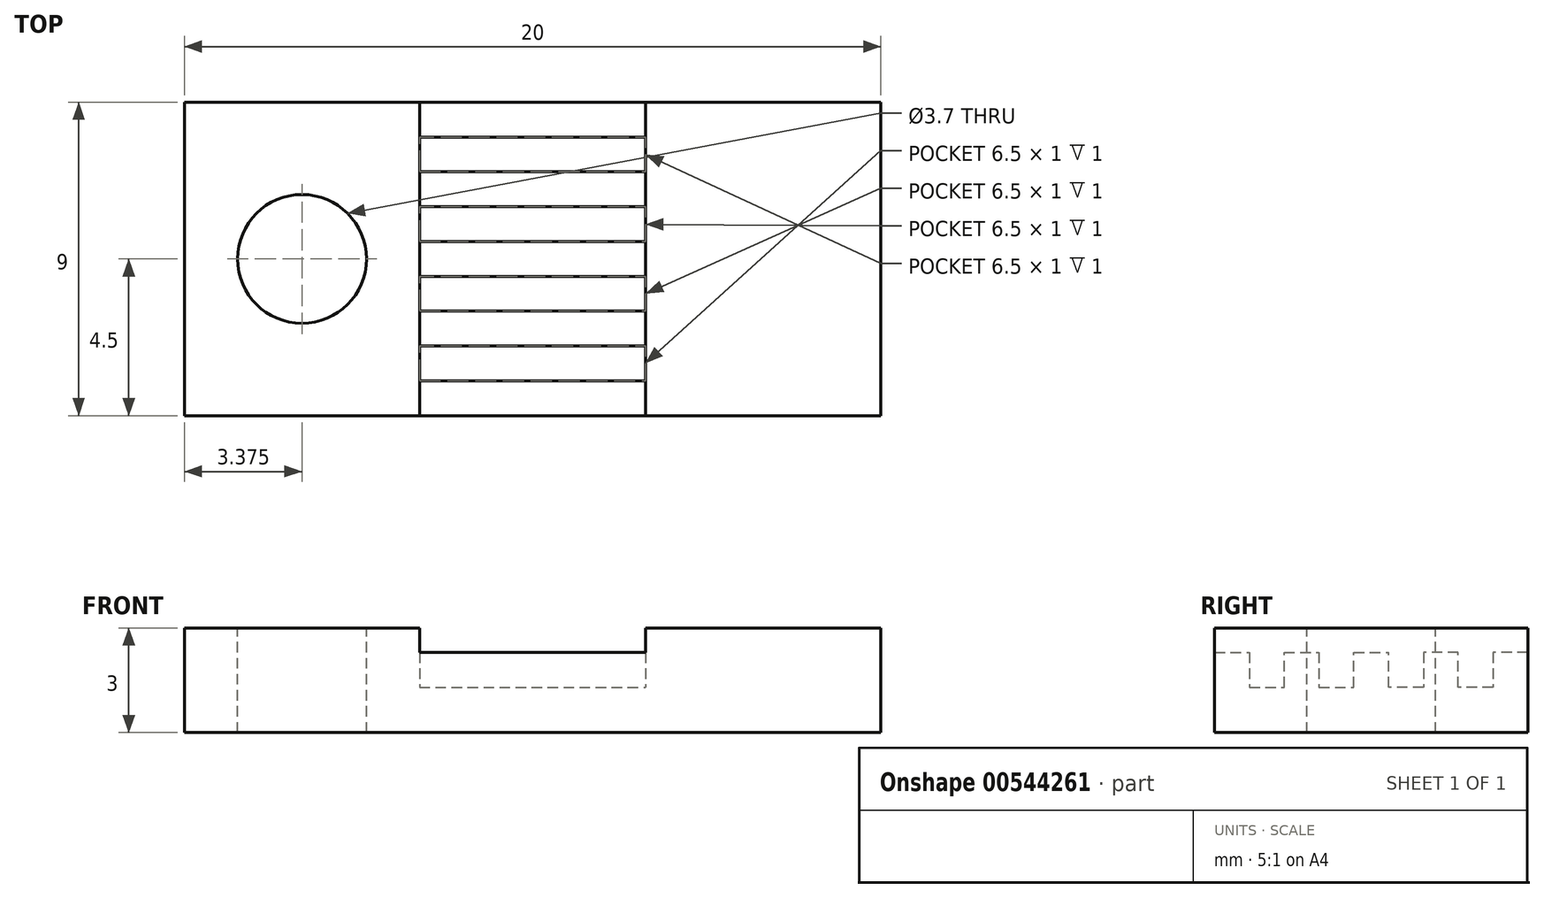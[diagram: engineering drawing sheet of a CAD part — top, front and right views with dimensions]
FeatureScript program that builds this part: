
annotation { "Feature Type Name" : "Feature", "Feature Type Description" : "" }
export const myFeature = defineFeature(function(context is Context, id is Id, definition is map)
    precondition{}
    {
        {
            var Q0;
            Q0=qCreatedBy(makeId("Top.planeOp"),FACE);
            var sketch = newSketch(context, id + "F0", { "sketchPlane" : qUnion([Q0])});
            skLineSegment(sketch, "E0.bottom", {"start": v(10, 4.5) * mm, "end": v(-10, 4.5) * mm});
            skLineSegment(sketch, "E0.top", {"start": v(10, -4.5) * mm, "end": v(-10, -4.5) * mm});
            skLineSegment(sketch, "E0.left", {"start": v(10, 4.5) * mm, "end": v(10, -4.5) * mm});
            skLineSegment(sketch, "E0.right", {"start": v(-10, 4.5) * mm, "end": v(-10, -4.5) * mm});
            skPoint(sketch, "E0.middle", {"position": v(0, 0) * mm});
            skSolve(sketch);
        }
        {
            var Q0;
            Q0=makeQuery(id+"F0.imprint","IMPRINT",FACE,{"disambiguationData":[TD([[makeQuery(id+"F0.imprint","IMPRINT",EDGE,{"derivedFrom":sQuery(id+"F0.wireOp",EDGE,"E0.bottom")}),1.0]])]});
            extrude(context, id + "F1", {"entities" : qUnion([Q0]), "depth" : 3 * mm, "offsetDistance" : 25 * mm});
        }
        {
            var Q0;
            Q0=qCreatedBy(makeId("Right.planeOp"),FACE);
            var sketch = newSketch(context, id + "F2", { "sketchPlane" : qUnion([Q0])});
            skLineSegment(sketch, "E1", {"start": v(0, 0) * mm, "end": v(0, 3) * mm, "construction": true});
            skLineSegment(sketch, "E2", {"start": v(0, 3) * mm, "end": v(-4.5, 3) * mm});
            skLineSegment(sketch, "E3", {"start": v(-4.5, 3) * mm, "end": v(-4.5, 2.3) * mm});
            skLineSegment(sketch, "E4", {"start": v(-4.5, 2.3) * mm, "end": v(-3.5, 2.3) * mm});
            skLineSegment(sketch, "E5", {"start": v(-3.5, 2.3) * mm, "end": v(-3.5, 1.3) * mm});
            skLineSegment(sketch, "E6", {"start": v(-3.5, 1.3) * mm, "end": v(-2.5, 1.3) * mm});
            skLineSegment(sketch, "E7", {"start": v(-2.5, 1.3) * mm, "end": v(-2.5, 2.3) * mm});
            skLineSegment(sketch, "E8", {"start": v(-2.5, 2.3) * mm, "end": v(-1.5, 2.3) * mm});
            skLineSegment(sketch, "E9", {"start": v(-1.5, 2.3) * mm, "end": v(-1.5, 1.3) * mm});
            skLineSegment(sketch, "E10", {"start": v(-1.5, 1.3) * mm, "end": v(-0.5, 1.3) * mm});
            skLineSegment(sketch, "E11", {"start": v(-0.5, 1.3) * mm, "end": v(-0.5, 2.3) * mm});
            skLineSegment(sketch, "E12", {"start": v(-0.5, 2.3) * mm, "end": v(0, 2.3) * mm});
            skLineSegment(sketch, "E13.MirrorCS", {"start": v(4.5, 3) * mm, "end": v(4.5, 2.3) * mm});
            skLineSegment(sketch, "E14.MirrorCS", {"start": v(1.5, 1.3) * mm, "end": v(0.5, 1.3) * mm});
            skLineSegment(sketch, "E15.MirrorCS", {"start": v(1.5, 2.3) * mm, "end": v(1.5, 1.3) * mm});
            skLineSegment(sketch, "E16.MirrorCS", {"start": v(2.5, 1.3) * mm, "end": v(2.5, 2.3) * mm});
            skLineSegment(sketch, "E17.MirrorCS", {"start": v(0, 3) * mm, "end": v(4.5, 3) * mm});
            skLineSegment(sketch, "E18.MirrorCS", {"start": v(0.5, 1.3) * mm, "end": v(0.5, 2.3) * mm});
            skLineSegment(sketch, "E19.MirrorCS", {"start": v(2.5, 2.3) * mm, "end": v(1.5, 2.3) * mm});
            skLineSegment(sketch, "E20.MirrorCS", {"start": v(0.5, 2.3) * mm, "end": v(0, 2.3) * mm});
            skLineSegment(sketch, "E21.MirrorCS", {"start": v(4.5, 2.3) * mm, "end": v(3.5, 2.3) * mm});
            skLineSegment(sketch, "E22.MirrorCS", {"start": v(3.5, 1.3) * mm, "end": v(2.5, 1.3) * mm});
            skLineSegment(sketch, "E23.MirrorCS", {"start": v(3.5, 2.3) * mm, "end": v(3.5, 1.3) * mm});
            skSolve(sketch);
        }
        {
            var Q0;
            Q0=makeQuery(id+"F2.imprint","IMPRINT",FACE,{"disambiguationData":[TD([[makeQuery(id+"F2.imprint","IMPRINT",EDGE,{"derivedFrom":sQuery(id+"F2.wireOp",EDGE,"E2")}),1.0]])]});
            extrude(context, id + "F3", {"entities" : qUnion([Q0]), "operationType" : NewBodyOperationType.REMOVE, "endBound" : BoundingType.SYMMETRIC, "oppositeDirection" : true, "depth" : 6.5 * mm, "offsetDistance" : 25 * mm});
        }
        {
            var Q0;
            {var subQ0=sQuery(id+"F0.wireOp",EDGE,"E0.bottom");var subQ1=sQuery(id+"F0.wireOp",EDGE,"E0.right");var subQ2=sQuery(id+"F0.wireOp",EDGE,"E0.top");Q0=makeQuery(id+"F3.boolean.opBoolean","SPLIT",FACE,{"disambiguationData":[TD([makeQuery(id+"F1.opExtrude","SWEPT_FACE",FACE,{"disambiguationData":[OSD([subQ1])]})])],"derivedFrom":makeQuery(id+"F1.opExtrude","CAP_FACE",FACE,{"disambiguationData":[OSD([subQ0,subQ2,sQuery(id+"F0.wireOp",EDGE,"E0.left"),subQ1])],"isStart":false})});}
            var sketch = newSketch(context, id + "F4", { "sketchPlane" : qUnion([Q0])});
            skLineSegment(sketch, "E24", {"start": v(0, 0) * mm, "end": v(0, 5.16) * mm, "construction": true});
            skCircle(sketch, "E25", {"center": v(-6.63, 0) * mm, "radius": 1.85 * mm});
            skCircle(sketch, "E26.MirrorC", {"center": v(6.63, 0) * mm, "radius": 1.85 * mm});
            skSolve(sketch);
        }
        {
            var Q0;
            Q0=makeQuery(id+"F4.imprint","IMPRINT",FACE,{"disambiguationData":[TD([[makeQuery(id+"F4.imprint","IMPRINT",EDGE,{"derivedFrom":sQuery(id+"F4.wireOp",EDGE,"E25")}),1.0]])]});
            var Q1;
            Q1=makeQuery(id+"F4.imprint","IMPRINT",FACE,{"disambiguationData":[TD([[makeQuery(id+"F4.imprint","IMPRINT",EDGE,{"derivedFrom":sQuery(id+"F4.wireOp",EDGE,"E26.MirrorC")}),-1.0]])]});
            extrude(context, id + "F5", {"entities" : qUnion([Q0, Q1]), "operationType" : NewBodyOperationType.REMOVE, "oppositeDirection" : true, "depth" : 25 * mm, "offsetDistance" : 25 * mm});
        }
    });
